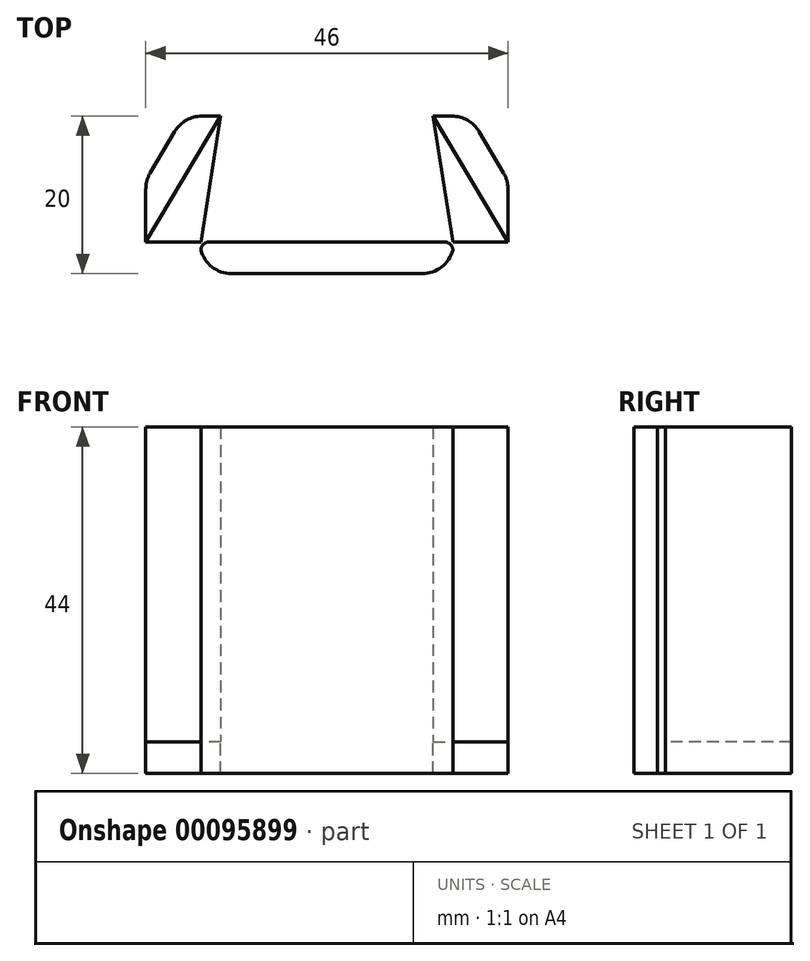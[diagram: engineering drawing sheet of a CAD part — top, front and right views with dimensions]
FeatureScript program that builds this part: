
annotation { "Feature Type Name" : "Feature", "Feature Type Description" : "" }
export const myFeature = defineFeature(function(context is Context, id is Id, definition is map)
    precondition{}
    {
        {
            var Q0;
            Q0=qCreatedBy(makeId("Top.planeOp"),FACE);
            var sketch = newSketch(context, id + "F0", { "sketchPlane" : qUnion([Q0])});
            skLineSegment(sketch, "E0.bottom", {"start": v(-23, -8) * mm, "end": v(23, -8) * mm});
            skLineSegment(sketch, "E0.top", {"start": v(-23, 8) * mm, "end": v(23, 8) * mm});
            skLineSegment(sketch, "E0.left", {"start": v(-23, -8) * mm, "end": v(-23, 8) * mm});
            skLineSegment(sketch, "E0.right", {"start": v(23, -8) * mm, "end": v(23, 8) * mm});
            skPoint(sketch, "E0.middle", {"position": v(0, 0) * mm});
            skLineSegment(sketch, "E1.bottom", {"start": v(27, -12) * mm, "end": v(-27, -12) * mm});
            skLineSegment(sketch, "E1.top", {"start": v(27, 12) * mm, "end": v(-27, 12) * mm});
            skLineSegment(sketch, "E1.left", {"start": v(27, -12) * mm, "end": v(27, 12) * mm});
            skLineSegment(sketch, "E1.right", {"start": v(-27, -12) * mm, "end": v(-27, 12) * mm});
            skLineSegment(sketch, "E2", {"start": v(0, 0) * mm, "end": v(0, 31.1) * mm, "construction": true});
            skLineSegment(sketch, "E3", {"start": v(-13.5, 8) * mm, "end": v(13.5, 8) * mm});
            skPoint(sketch, "E4", {"position": v(0, 8) * mm});
            skLineSegment(sketch, "E5", {"start": v(-13.5, 8) * mm, "end": v(-23, -8) * mm});
            skLineSegment(sketch, "E6", {"start": v(13.5, 8) * mm, "end": v(23, -8) * mm});
            skLineSegment(sketch, "E7", {"start": v(-15.78, 12) * mm, "end": v(-27, -6.9) * mm});
            skLineSegment(sketch, "E8.MirrorCS", {"start": v(15.78, 12) * mm, "end": v(27, -6.9) * mm});
            skLineSegment(sketch, "E9", {"start": v(0, 0) * mm, "end": v(0, -8) * mm, "construction": true});
            skLineSegment(sketch, "E10", {"start": v(0, -8) * mm, "end": v(0, -12) * mm, "construction": true});
            skLineSegment(sketch, "E11.bottom", {"start": v(16, -12) * mm, "end": v(-16, -12) * mm});
            skLineSegment(sketch, "E11.top", {"start": v(16, -8) * mm, "end": v(-16, -8) * mm});
            skLineSegment(sketch, "E11.left", {"start": v(16, -12) * mm, "end": v(16, -8) * mm});
            skLineSegment(sketch, "E11.right", {"start": v(-16, -12) * mm, "end": v(-16, -8) * mm});
            skPoint(sketch, "E11.middle", {"position": v(0, -10) * mm});
            skLineSegment(sketch, "E12", {"start": v(-13.5, 8) * mm, "end": v(-16, -8) * mm});
            skLineSegment(sketch, "E13", {"start": v(13.5, 8) * mm, "end": v(16, -8) * mm});
            skSolve(sketch);
        }
        {
            var Q0;
            Q0=makeQuery(id+"F0.imprint","IMPRINT",FACE,{"disambiguationData":[TD([[makeQuery(id+"F0.imprint","IMPRINT",EDGE,{"derivedFrom":sQuery(id+"F0.wireOp",EDGE,"E0.bottom")}),-1.0]])]});
            var Q1;
            Q1=makeQuery(id+"F0.imprint","IMPRINT",FACE,{"disambiguationData":[TD([[makeQuery(id+"F0.imprint","IMPRINT",EDGE,{"derivedFrom":sQuery(id+"F0.wireOp",EDGE,"E0.bottom")}),1.0]])]});
            var Q2;
            {var subQ0=sQuery(id+"F0.wireOp",EDGE,"E5");Q2=makeQuery(id+"F0.imprint","IMPRINT",FACE,{"disambiguationData":[TD([[makeQuery(id+"F0.imprint","IMPRINT",EDGE,{"derivedFrom":subQ0}),-1.0]])]});}
            var Q3;
            {var subQ5=sQuery(id+"F0.wireOp",EDGE,"E3");Q3=makeQuery(id+"F0.imprint","IMPRINT",FACE,{"disambiguationData":[TD([[makeQuery(id+"F0.imprint","IMPRINT",EDGE,{"derivedFrom":subQ5}),1.0]])]});}
            var Q4;
            {var subQ0=sQuery(id+"F0.wireOp",EDGE,"E6");Q4=makeQuery(id+"F0.imprint","IMPRINT",FACE,{"disambiguationData":[TD([[makeQuery(id+"F0.imprint","IMPRINT",EDGE,{"derivedFrom":subQ0}),1.0]])]});}
            extrude(context, id + "F1", {"entities" : qUnion([Q0, Q1, Q2, Q3, Q4]), "oppositeDirection" : true, "depth" : 4 * mm});
        }
        {
            var Q0;
            {var subQ7=sQuery(id+"F0.wireOp",EDGE,"E0.bottom");Q0=makeQuery(id+"F0.imprint","IMPRINT",FACE,{"disambiguationData":[TD([[makeQuery(id+"F0.imprint","IMPRINT",EDGE,{"derivedFrom":subQ7}),-1.0]])]});}
            var Q1;
            {var subQ5=sQuery(id+"F0.wireOp",EDGE,"E3");Q1=makeQuery(id+"F0.imprint","IMPRINT",FACE,{"disambiguationData":[TD([[makeQuery(id+"F0.imprint","IMPRINT",EDGE,{"derivedFrom":subQ5}),1.0]])]});}
            var Q2;
            {var subQ0=sQuery(id+"F0.wireOp",EDGE,"E5");Q2=makeQuery(id+"F0.imprint","IMPRINT",FACE,{"disambiguationData":[TD([[makeQuery(id+"F0.imprint","IMPRINT",EDGE,{"derivedFrom":subQ0}),-1.0]])]});}
            var Q3;
            {var subQ0=sQuery(id+"F0.wireOp",EDGE,"E6");Q3=makeQuery(id+"F0.imprint","IMPRINT",FACE,{"disambiguationData":[TD([[makeQuery(id+"F0.imprint","IMPRINT",EDGE,{"derivedFrom":subQ0}),1.0]])]});}
            extrude(context, id + "F2", {"entities" : qUnion([Q0, Q1, Q2, Q3]), "operationType" : NewBodyOperationType.ADD, "depth" : 40 * mm});
        }
        {
            var Q0;
            Q0=makeQuery(id+"F2.opExtrude","SWEPT_EDGE",EDGE,{"disambiguationData":[OSD([sQuery(id+"F0.wireOp",EDGE,"E0.top"),sQuery(id+"F0.wireOp",EDGE,"E3"),sQuery(id+"F0.wireOp",EDGE,"E5"),sQuery(id+"F0.wireOp",EDGE,"E12")])]});
            var Q1;
            Q1=makeQuery(id+"F2.opExtrude","SWEPT_EDGE",EDGE,{"disambiguationData":[OSD([sQuery(id+"F0.wireOp",EDGE,"E0.top"),sQuery(id+"F0.wireOp",EDGE,"E3"),sQuery(id+"F0.wireOp",EDGE,"E6"),sQuery(id+"F0.wireOp",EDGE,"E13")])]});
            var Q2;
            Q2=makeQuery(id+"F2.opExtrude","SWEPT_EDGE",EDGE,{"disambiguationData":[OSD([sQuery(id+"F0.wireOp",EDGE,"E0.bottom"),sQuery(id+"F0.wireOp",EDGE,"E0.right"),sQuery(id+"F0.wireOp",EDGE,"E6")])]});
            var Q3;
            Q3=makeQuery(id+"F2.opExtrude","SWEPT_EDGE",EDGE,{"disambiguationData":[OSD([sQuery(id+"F0.wireOp",EDGE,"E0.bottom"),sQuery(id+"F0.wireOp",EDGE,"E0.left"),sQuery(id+"F0.wireOp",EDGE,"E5")])]});
            var Q4;
            Q4=makeQuery(id+"F2.opExtrude","SWEPT_EDGE",EDGE,{"disambiguationData":[OSD([sQuery(id+"F0.wireOp",EDGE,"E0.bottom"),sQuery(id+"F0.wireOp",EDGE,"E11.top"),sQuery(id+"F0.wireOp",EDGE,"E11.right"),sQuery(id+"F0.wireOp",EDGE,"E12")])]});
            var Q5;
            Q5=makeQuery(id+"F2.opExtrude","SWEPT_EDGE",EDGE,{"disambiguationData":[OSD([sQuery(id+"F0.wireOp",EDGE,"E0.bottom"),sQuery(id+"F0.wireOp",EDGE,"E11.top"),sQuery(id+"F0.wireOp",EDGE,"E11.left"),sQuery(id+"F0.wireOp",EDGE,"E13")])]});
            fillet(context, id + "F3", {"entities" : qUnion([Q0, Q1, Q2, Q3, Q4, Q5]), "radius" : 1 * mm, "tangentPropagation" : true, "allowEdgeOverflow" : false});
        }
        {
            var Q0;
            {var subQ0=sQuery(id+"F0.wireOp",EDGE,"E1.left");var subQ1=sQuery(id+"F0.wireOp",EDGE,"E1.bottom");Q0=makeQuery(id+"F2.boolean.opBoolean","MERGE",EDGE,{"derivedFrom":[makeQuery(id+"F1.opExtrude","SWEPT_EDGE",EDGE,{"disambiguationData":[OSD([subQ1,subQ0])]}),makeQuery(id+"F2.opExtrude","SWEPT_EDGE",EDGE,{"disambiguationData":[OSD([subQ1,subQ0])]})]});}
            var Q1;
            {var subQ0=sQuery(id+"F0.wireOp",EDGE,"E8.MirrorCS");var subQ1=sQuery(id+"F0.wireOp",EDGE,"E1.left");Q1=makeQuery(id+"F2.boolean.opBoolean","MERGE",EDGE,{"derivedFrom":[makeQuery(id+"F1.opExtrude","SWEPT_EDGE",EDGE,{"disambiguationData":[OSD([subQ1,subQ0])]}),makeQuery(id+"F2.opExtrude","SWEPT_EDGE",EDGE,{"disambiguationData":[OSD([subQ1,subQ0])]})]});}
            var Q2;
            {var subQ0=sQuery(id+"F0.wireOp",EDGE,"E7");var subQ1=sQuery(id+"F0.wireOp",EDGE,"E1.right");Q2=makeQuery(id+"F2.boolean.opBoolean","MERGE",EDGE,{"derivedFrom":[makeQuery(id+"F1.opExtrude","SWEPT_EDGE",EDGE,{"disambiguationData":[OSD([subQ1,subQ0])]}),makeQuery(id+"F2.opExtrude","SWEPT_EDGE",EDGE,{"disambiguationData":[OSD([subQ1,subQ0])]})]});}
            var Q3;
            {var subQ0=sQuery(id+"F0.wireOp",EDGE,"E1.right");var subQ1=sQuery(id+"F0.wireOp",EDGE,"E1.bottom");Q3=makeQuery(id+"F2.boolean.opBoolean","MERGE",EDGE,{"derivedFrom":[makeQuery(id+"F1.opExtrude","SWEPT_EDGE",EDGE,{"disambiguationData":[OSD([subQ1,subQ0])]}),makeQuery(id+"F2.opExtrude","SWEPT_EDGE",EDGE,{"disambiguationData":[OSD([subQ1,subQ0])]})]});}
            var Q4;
            {var subQ0=sQuery(id+"F0.wireOp",EDGE,"E11.left");var subQ1=sQuery(id+"F0.wireOp",EDGE,"E11.bottom");var subQ2=sQuery(id+"F0.wireOp",EDGE,"E1.bottom");Q4=makeQuery(id+"F2.boolean.opBoolean","MERGE",EDGE,{"derivedFrom":[makeQuery(id+"F1.opExtrude","SWEPT_EDGE",EDGE,{"disambiguationData":[OSD([subQ2,subQ1,subQ0])]}),makeQuery(id+"F2.opExtrude","SWEPT_EDGE",EDGE,{"disambiguationData":[OSD([subQ2,subQ1,subQ0])]})]});}
            var Q5;
            {var subQ0=sQuery(id+"F0.wireOp",EDGE,"E11.right");var subQ1=sQuery(id+"F0.wireOp",EDGE,"E11.bottom");var subQ2=sQuery(id+"F0.wireOp",EDGE,"E1.bottom");Q5=makeQuery(id+"F2.boolean.opBoolean","MERGE",EDGE,{"derivedFrom":[makeQuery(id+"F1.opExtrude","SWEPT_EDGE",EDGE,{"disambiguationData":[OSD([subQ2,subQ1,subQ0])]}),makeQuery(id+"F2.opExtrude","SWEPT_EDGE",EDGE,{"disambiguationData":[OSD([subQ2,subQ1,subQ0])]})]});}
            var Q6;
            {var subQ0=sQuery(id+"F0.wireOp",EDGE,"E7");var subQ1=sQuery(id+"F0.wireOp",EDGE,"E1.top");Q6=makeQuery(id+"F2.boolean.opBoolean","MERGE",EDGE,{"derivedFrom":[makeQuery(id+"F1.opExtrude","SWEPT_EDGE",EDGE,{"disambiguationData":[OSD([subQ1,subQ0])]}),makeQuery(id+"F2.opExtrude","SWEPT_EDGE",EDGE,{"disambiguationData":[OSD([subQ1,subQ0])]})]});}
            var Q7;
            {var subQ0=sQuery(id+"F0.wireOp",EDGE,"E8.MirrorCS");var subQ1=sQuery(id+"F0.wireOp",EDGE,"E1.top");Q7=makeQuery(id+"F2.boolean.opBoolean","MERGE",EDGE,{"derivedFrom":[makeQuery(id+"F1.opExtrude","SWEPT_EDGE",EDGE,{"disambiguationData":[OSD([subQ1,subQ0])]}),makeQuery(id+"F2.opExtrude","SWEPT_EDGE",EDGE,{"disambiguationData":[OSD([subQ1,subQ0])]})]});}
            fillet(context, id + "F4", {"entities" : qUnion([Q0, Q1, Q2, Q3, Q4, Q5, Q6, Q7]), "radius" : 4 * mm, "tangentPropagation" : true, "allowEdgeOverflow" : false});
        }
    });
